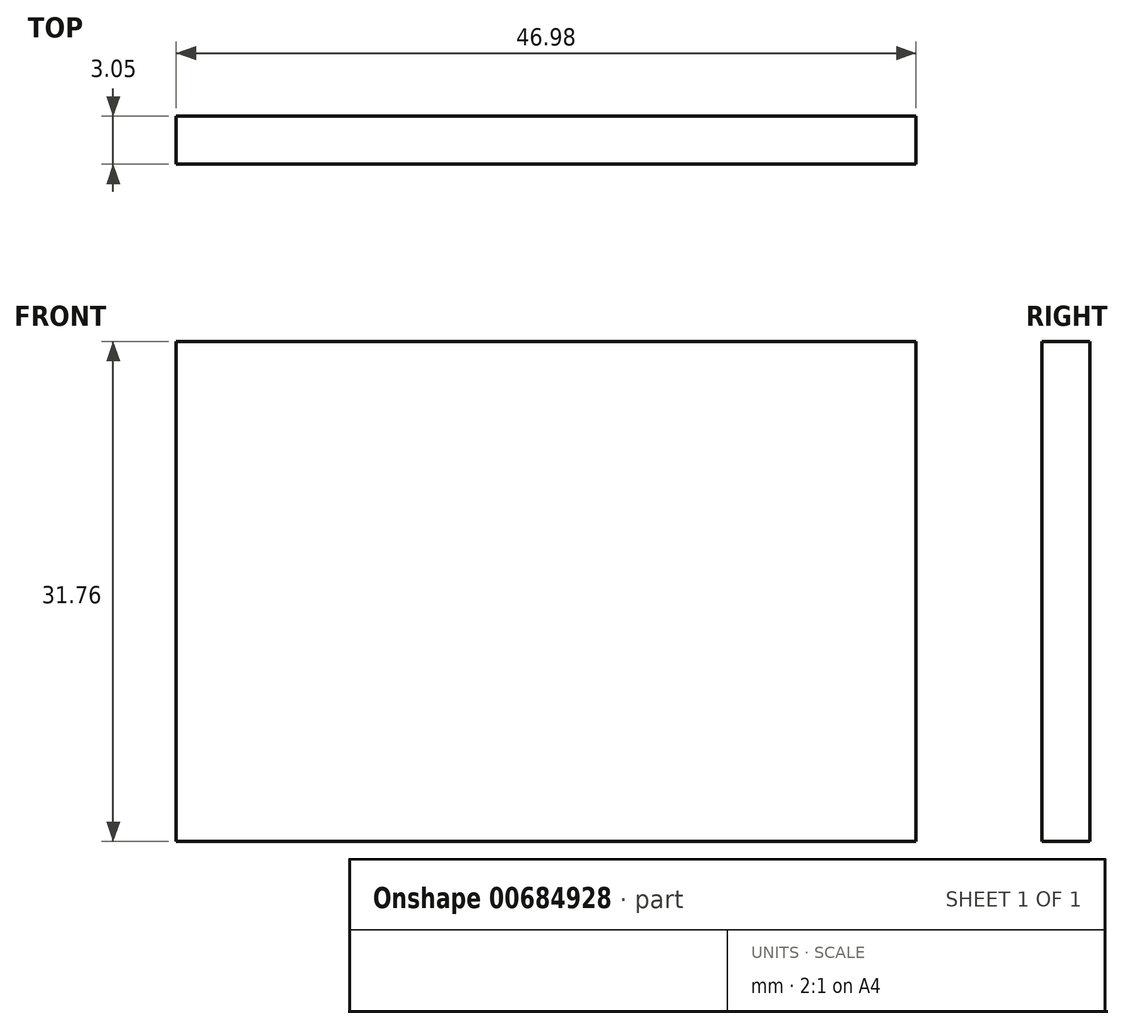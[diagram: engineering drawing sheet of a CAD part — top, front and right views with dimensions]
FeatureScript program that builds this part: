
annotation { "Feature Type Name" : "Feature", "Feature Type Description" : "" }
export const myFeature = defineFeature(function(context is Context, id is Id, definition is map)
    precondition{}
    {
        {
            var Q0;
            Q0=qCreatedBy(makeId("Front.planeOp"),FACE);
            var sketch = newSketch(context, id + "F0", { "sketchPlane" : qUnion([Q0])});
            skLineSegment(sketch, "E0.bottom", {"start": v(23.5, 15.88) * mm, "end": v(-23.5, 15.88) * mm});
            skLineSegment(sketch, "E0.top", {"start": v(23.5, -15.88) * mm, "end": v(-23.5, -15.88) * mm});
            skLineSegment(sketch, "E0.left", {"start": v(23.5, 15.88) * mm, "end": v(23.5, -15.88) * mm});
            skLineSegment(sketch, "E0.right", {"start": v(-23.5, 15.88) * mm, "end": v(-23.5, -15.88) * mm});
            skPoint(sketch, "E0.middle", {"position": v(0, 0) * mm});
            skSolve(sketch);
        }
        {
            var Q0;
            Q0 = qSketchRegion(id + "F0", true);
            extrude(context, id + "F1", {"entities" : qUnion([Q0]), "depth" : 3.05 * mm, "offsetDistance" : 25.4 * mm});
        }
    });
